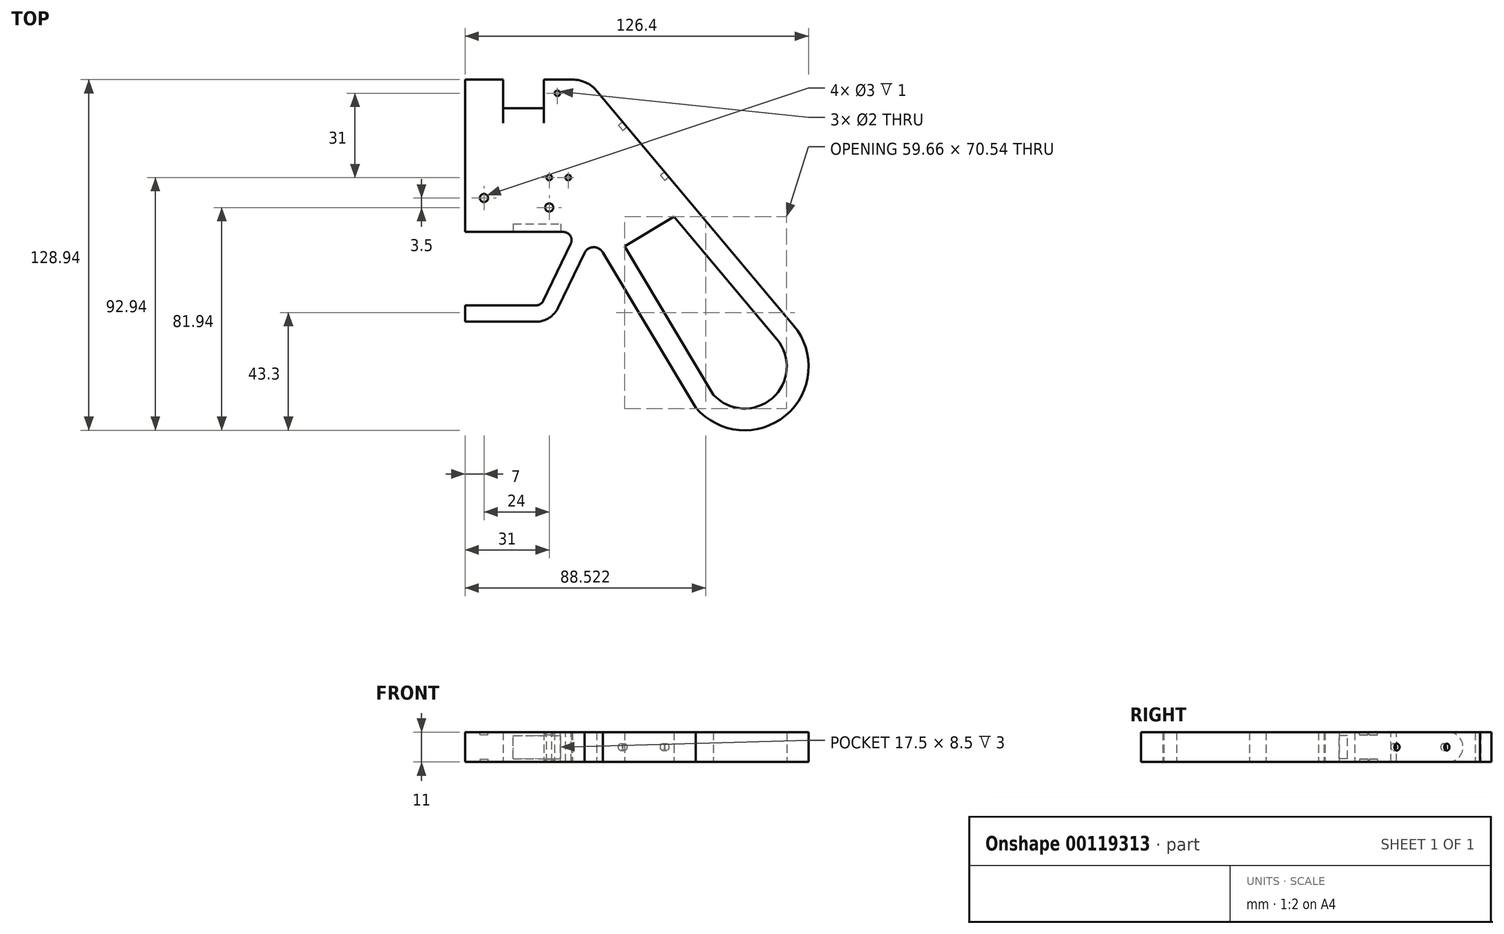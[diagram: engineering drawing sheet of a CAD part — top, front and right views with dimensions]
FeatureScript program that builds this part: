
annotation { "Feature Type Name" : "Feature", "Feature Type Description" : "" }
export const myFeature = defineFeature(function(context is Context, id is Id, definition is map)
    precondition{}
    {
        {
            var Q0;
            Q0=qCreatedBy(makeId("Top.planeOp"),FACE);
            var sketch = newSketch(context, id + "F0", { "sketchPlane" : qUnion([Q0])});
            skLineSegment(sketch, "E0", {"start": v(0, 0) * mm, "end": v(0, 56) * mm});
            skLineSegment(sketch, "E1", {"start": v(0, -27) * mm, "end": v(0, -33) * mm});
            skLineSegment(sketch, "E2", {"start": v(0, -33) * mm, "end": v(26.11, -33) * mm});
            skLineSegment(sketch, "E3", {"start": v(0, -27) * mm, "end": v(26.11, -27) * mm});
            skLineSegment(sketch, "E4", {"start": v(0, 56) * mm, "end": v(14, 56) * mm});
            skLineSegment(sketch, "E5", {"start": v(0, 0) * mm, "end": v(36.23, 0) * mm});
            skLineSegment(sketch, "E6", {"start": v(28.82, -25.3) * mm, "end": v(38.93, -4.3) * mm});
            skLineSegment(sketch, "E7.0", {"start": v(34.22, -27.9) * mm, "end": v(43.96, -7.7) * mm});
            skArc(sketch, "E8.filletArc", {"start": v(38.93, -4.3) * mm, "mid": v(38.77, -1.4) * mm, "end": v(36.23, 0) * mm});
            skArc(sketch, "E9.filletArc", {"start": v(26.11, -27) * mm, "mid": v(27.71, -26.54) * mm, "end": v(28.82, -25.3) * mm});
            skArc(sketch, "E10.0", {"start": v(26.11, -33) * mm, "mid": v(30.9, -31.62) * mm, "end": v(34.22, -27.9) * mm});
            skLineSegment(sketch, "E11.0", {"start": v(14, 40) * mm, "end": v(14, 56) * mm});
            skLineSegment(sketch, "E12.0", {"start": v(29, 40) * mm, "end": v(29, 56) * mm});
            skLineSegment(sketch, "E13.0", {"start": v(14, 40) * mm, "end": v(29, 40) * mm});
            skLineSegment(sketch, "E14.trimOffspring", {"start": v(29, 56) * mm, "end": v(39.5, 56) * mm});
            skLineSegment(sketch, "E15", {"start": v(48.5, 51.83) * mm, "end": v(120.9, -34.35) * mm});
            skLineSegment(sketch, "E16", {"start": v(84.94, -64.56) * mm, "end": v(50.76, -7.6) * mm});
            skArc(sketch, "E17", {"start": v(84.94, -64.56) * mm, "mid": v(118.02, -67.44) * mm, "end": v(120.9, -34.35) * mm});
            skArc(sketch, "E18", {"start": v(48.5, 51.83) * mm, "mid": v(44.49, 54.96) * mm, "end": v(39.5, 56) * mm});
            skPoint(sketch, "E19.orphan", {"position": v(46.5, 54.22) * mm});
            skCircle(sketch, "E20", {"center": v(34, 51) * mm, "radius": 1 * mm});
            skArc(sketch, "E21", {"start": v(50.76, -7.6) * mm, "mid": v(47.33, -5.6) * mm, "end": v(43.96, -7.7) * mm});
            skSolve(sketch);
        }
        {
            var Q0;
            Q0 = qSketchRegion(id + "F0", true);
            extrude(context, id + "F1", {"entities" : qUnion([Q0]), "endBound" : BoundingType.SYMMETRIC, "depth" : 11 * mm});
        }
        {
            var Q0;
            Q0=makeQuery(id+"F1.opExtrude","SWEPT_FACE",FACE,{"disambiguationData":[OSD([sQuery(id+"F0.wireOp",EDGE,"E12.0")])]});
            var sketch = newSketch(context, id + "F2", { "sketchPlane" : qUnion([Q0])});
            skLineSegment(sketch, "E22", {"start": v(-40, -5.5) * mm, "end": v(-40, 5.5) * mm});
            skArc(sketch, "E23", {"start": v(-40, 5.5) * mm, "mid": v(-45.5, 0) * mm, "end": v(-40, -5.5) * mm});
            skSolve(sketch);
        }
        {
            var Q0;
            Q0 = qSketchRegion(id + "F2", true);
            extrude(context, id + "F3", {"entities" : qUnion([Q0]), "operationType" : NewBodyOperationType.ADD, "depth" : 25 * mm});
        }
        {
            var Q0;
            Q0=makeQuery(id+"F1.opExtrude","CAP_FACE",FACE,{"disambiguationData":[OSD([sQuery(id+"F0.wireOp",EDGE,"E0"),sQuery(id+"F0.wireOp",EDGE,"E1"),sQuery(id+"F0.wireOp",EDGE,"E2"),sQuery(id+"F0.wireOp",EDGE,"E3"),sQuery(id+"F0.wireOp",EDGE,"E4"),sQuery(id+"F0.wireOp",EDGE,"E5"),sQuery(id+"F0.wireOp",EDGE,"E6"),sQuery(id+"F0.wireOp",EDGE,"E7.0"),sQuery(id+"F0.wireOp",EDGE,"E8.filletArc"),sQuery(id+"F0.wireOp",EDGE,"E9.filletArc"),sQuery(id+"F0.wireOp",EDGE,"E10.0"),sQuery(id+"F0.wireOp",EDGE,"E11.0"),sQuery(id+"F0.wireOp",EDGE,"E12.0"),sQuery(id+"F0.wireOp",EDGE,"E13.0"),sQuery(id+"F0.wireOp",EDGE,"E14.trimOffspring"),sQuery(id+"F0.wireOp",EDGE,"E15"),sQuery(id+"F0.wireOp",EDGE,"E16"),sQuery(id+"F0.wireOp",EDGE,"3d227ca1-747b-497a-97d5-58212d2cf885.filletArc"),sQuery(id+"F0.wireOp",EDGE,"E17"),sQuery(id+"F0.wireOp",EDGE,"E18"),sQuery(id+"F0.wireOp",EDGE,"E20")])],"isStart":false});
            var sketch = newSketch(context, id + "F4", { "sketchPlane" : qUnion([Q0])});
            skLineSegment(sketch, "E24", {"start": v(0, 56) * mm, "end": v(60.5, 56) * mm, "construction": true});
            skPoint(sketch, "E24.endSnap0", {"position": v(34.25, 56) * mm});
            skLineSegment(sketch, "E25", {"start": v(0, 56) * mm, "end": v(0, -13.4) * mm, "construction": true});
            skCircle(sketch, "E26", {"center": v(31, 20) * mm, "radius": 1 * mm});
            skCircle(sketch, "E27", {"center": v(38, 20) * mm, "radius": 1 * mm});
            skSolve(sketch);
        }
        {
            var Q0;
            Q0 = qSketchRegion(id + "F4", true);
            extrude(context, id + "F5", {"entities" : qUnion([Q0]), "operationType" : NewBodyOperationType.REMOVE, "endBound" : BoundingType.THROUGH_ALL, "oppositeDirection" : true, "depth" : 25 * mm});
        }
        {
            var Q0;
            Q0=makeQuery(id+"F1.opExtrude","SWEPT_FACE",FACE,{"disambiguationData":[OSD([sQuery(id+"F0.wireOp",EDGE,"E5")])]});
            var sketch = newSketch(context, id + "F6", { "sketchPlane" : qUnion([Q0])});
            skLineSegment(sketch, "E28", {"start": v(35.23, -4.25) * mm, "end": v(35.23, 4.25) * mm});
            skLineSegment(sketch, "E29.0", {"start": v(17.73, -4.25) * mm, "end": v(17.73, 4.25) * mm});
            skLineSegment(sketch, "E30.0", {"start": v(17.73, 4.25) * mm, "end": v(35.23, 4.25) * mm});
            skLineSegment(sketch, "E31.MirrorCS", {"start": v(17.73, -4.25) * mm, "end": v(35.23, -4.25) * mm});
            skSolve(sketch);
        }
        {
            var Q0;
            Q0 = qSketchRegion(id + "F6", true);
            extrude(context, id + "F7", {"entities" : qUnion([Q0]), "operationType" : NewBodyOperationType.REMOVE, "oppositeDirection" : true, "depth" : 3 * mm});
        }
        {
            var Q0;
            Q0=makeQuery(id+"F1.opExtrude","SWEPT_FACE",FACE,{"disambiguationData":[OSD([sQuery(id+"F0.wireOp",EDGE,"E15")])]});
            var sketch = newSketch(context, id + "F8", { "sketchPlane" : qUnion([Q0])});
            skCircle(sketch, "E32", {"center": v(-31.5, 0) * mm, "radius": 1.25 * mm});
            skCircle(sketch, "E33", {"center": v(-7.5, 0) * mm, "radius": 1.25 * mm});
            skSolve(sketch);
        }
        {
            var Q0;
            Q0 = qSketchRegion(id + "F8", true);
            extrude(context, id + "F9", {"entities" : qUnion([Q0]), "operationType" : NewBodyOperationType.REMOVE, "oppositeDirection" : true, "depth" : 2 * mm});
        }
        {
            var Q0;
            Q0=makeQuery(id+"F1.opExtrude","CAP_FACE",FACE,{"disambiguationData":[OSD([sQuery(id+"F0.wireOp",EDGE,"E0"),sQuery(id+"F0.wireOp",EDGE,"E1"),sQuery(id+"F0.wireOp",EDGE,"E2"),sQuery(id+"F0.wireOp",EDGE,"E3"),sQuery(id+"F0.wireOp",EDGE,"E4"),sQuery(id+"F0.wireOp",EDGE,"E5"),sQuery(id+"F0.wireOp",EDGE,"E6"),sQuery(id+"F0.wireOp",EDGE,"E7.0"),sQuery(id+"F0.wireOp",EDGE,"E8.filletArc"),sQuery(id+"F0.wireOp",EDGE,"E9.filletArc"),sQuery(id+"F0.wireOp",EDGE,"E10.0"),sQuery(id+"F0.wireOp",EDGE,"E11.0"),sQuery(id+"F0.wireOp",EDGE,"E12.0"),sQuery(id+"F0.wireOp",EDGE,"E13.0"),sQuery(id+"F0.wireOp",EDGE,"E14.trimOffspring"),sQuery(id+"F0.wireOp",EDGE,"E15"),sQuery(id+"F0.wireOp",EDGE,"E16"),sQuery(id+"F0.wireOp",EDGE,"E17"),sQuery(id+"F0.wireOp",EDGE,"E18"),sQuery(id+"F0.wireOp",EDGE,"E20"),sQuery(id+"F0.wireOp",EDGE,"E21")])],"isStart":false});
            var sketch = newSketch(context, id + "F10", { "sketchPlane" : qUnion([Q0])});
            skLineSegment(sketch, "E34", {"start": v(7, 86.3) * mm, "end": v(7, -32.77) * mm, "construction": true});
            skLineSegment(sketch, "E35", {"start": v(31, 65.41) * mm, "end": v(31, -4.92) * mm, "construction": true});
            skLineSegment(sketch, "E36.0", {"start": v(0, 9) * mm, "end": v(36.23, 9) * mm, "construction": true});
            skLineSegment(sketch, "E37.0", {"start": v(0, 12.5) * mm, "end": v(36.23, 12.5) * mm, "construction": true});
            skCircle(sketch, "E38", {"center": v(7, 12.5) * mm, "radius": 1.5 * mm});
            skCircle(sketch, "E39", {"center": v(31, 9) * mm, "radius": 1.5 * mm});
            skSolve(sketch);
        }
        {
            var Q0;
            Q0 = qSketchRegion(id + "F10", true);
            extrude(context, id + "F11", {"entities" : qUnion([Q0]), "operationType" : NewBodyOperationType.REMOVE, "oppositeDirection" : true, "depth" : 1 * mm});
        }
        {
            var Q0;
            Q0=makeQuery(id+"F1.opExtrude","CAP_FACE",FACE,{"disambiguationData":[OSD([sQuery(id+"F0.wireOp",EDGE,"E0"),sQuery(id+"F0.wireOp",EDGE,"E1"),sQuery(id+"F0.wireOp",EDGE,"E2"),sQuery(id+"F0.wireOp",EDGE,"E3"),sQuery(id+"F0.wireOp",EDGE,"E4"),sQuery(id+"F0.wireOp",EDGE,"E5"),sQuery(id+"F0.wireOp",EDGE,"E6"),sQuery(id+"F0.wireOp",EDGE,"E7.0"),sQuery(id+"F0.wireOp",EDGE,"E8.filletArc"),sQuery(id+"F0.wireOp",EDGE,"E9.filletArc"),sQuery(id+"F0.wireOp",EDGE,"E10.0"),sQuery(id+"F0.wireOp",EDGE,"E11.0"),sQuery(id+"F0.wireOp",EDGE,"E12.0"),sQuery(id+"F0.wireOp",EDGE,"E13.0"),sQuery(id+"F0.wireOp",EDGE,"E14.trimOffspring"),sQuery(id+"F0.wireOp",EDGE,"E15"),sQuery(id+"F0.wireOp",EDGE,"E16"),sQuery(id+"F0.wireOp",EDGE,"E17"),sQuery(id+"F0.wireOp",EDGE,"E18"),sQuery(id+"F0.wireOp",EDGE,"E20"),sQuery(id+"F0.wireOp",EDGE,"E21")])],"isStart":true});
            var sketch = newSketch(context, id + "F12", { "sketchPlane" : qUnion([Q0])});
            skCircle(sketch, "E40.0", {"center": v(7, -12.5) * mm, "radius": 1.5 * mm});
            skCircle(sketch, "E41.0", {"center": v(31, -9) * mm, "radius": 1.5 * mm});
            skSolve(sketch);
        }
        {
            var Q0;
            Q0 = qSketchRegion(id + "F12", true);
            extrude(context, id + "F13", {"entities" : qUnion([Q0]), "operationType" : NewBodyOperationType.REMOVE, "oppositeDirection" : true, "depth" : 1 * mm});
        }
        {
            var Q0;
            Q0=makeQuery(id+"F1.opExtrude","CAP_FACE",FACE,{"disambiguationData":[OSD([sQuery(id+"F0.wireOp",EDGE,"E0"),sQuery(id+"F0.wireOp",EDGE,"E1"),sQuery(id+"F0.wireOp",EDGE,"E2"),sQuery(id+"F0.wireOp",EDGE,"E3"),sQuery(id+"F0.wireOp",EDGE,"E4"),sQuery(id+"F0.wireOp",EDGE,"E5"),sQuery(id+"F0.wireOp",EDGE,"E6"),sQuery(id+"F0.wireOp",EDGE,"E7.0"),sQuery(id+"F0.wireOp",EDGE,"E8.filletArc"),sQuery(id+"F0.wireOp",EDGE,"E9.filletArc"),sQuery(id+"F0.wireOp",EDGE,"E10.0"),sQuery(id+"F0.wireOp",EDGE,"E11.0"),sQuery(id+"F0.wireOp",EDGE,"E12.0"),sQuery(id+"F0.wireOp",EDGE,"E13.0"),sQuery(id+"F0.wireOp",EDGE,"E14.trimOffspring"),sQuery(id+"F0.wireOp",EDGE,"E15"),sQuery(id+"F0.wireOp",EDGE,"E16"),sQuery(id+"F0.wireOp",EDGE,"E17"),sQuery(id+"F0.wireOp",EDGE,"E18"),sQuery(id+"F0.wireOp",EDGE,"E20"),sQuery(id+"F0.wireOp",EDGE,"E21")])],"isStart":true});
            var sketch = newSketch(context, id + "F14", { "sketchPlane" : qUnion([Q0])});
            skLineSegment(sketch, "E42.0", {"start": v(42.37, -46.69) * mm, "end": v(114.77, 39.5) * mm});
            skArc(sketch, "E43.0", {"start": v(91.06, 59.41) * mm, "mid": v(112.87, 61.31) * mm, "end": v(114.77, 39.5) * mm});
            skLineSegment(sketch, "E44.0", {"start": v(91.8, 60.44) * mm, "end": v(57.62, 3.49) * mm});
            skLineSegment(sketch, "E45.0", {"start": v(56.77, 6.42) * mm, "end": v(76.86, -5.63) * mm});
            skSolve(sketch);
        }
        {
            var Q0;
            Q0 = qSketchRegion(id + "F14", true);
            extrude(context, id + "F15", {"entities" : qUnion([Q0]), "operationType" : NewBodyOperationType.REMOVE, "oppositeDirection" : true, "depth" : 25 * mm, "offsetDistance" : 25 * mm});
        }
    });
